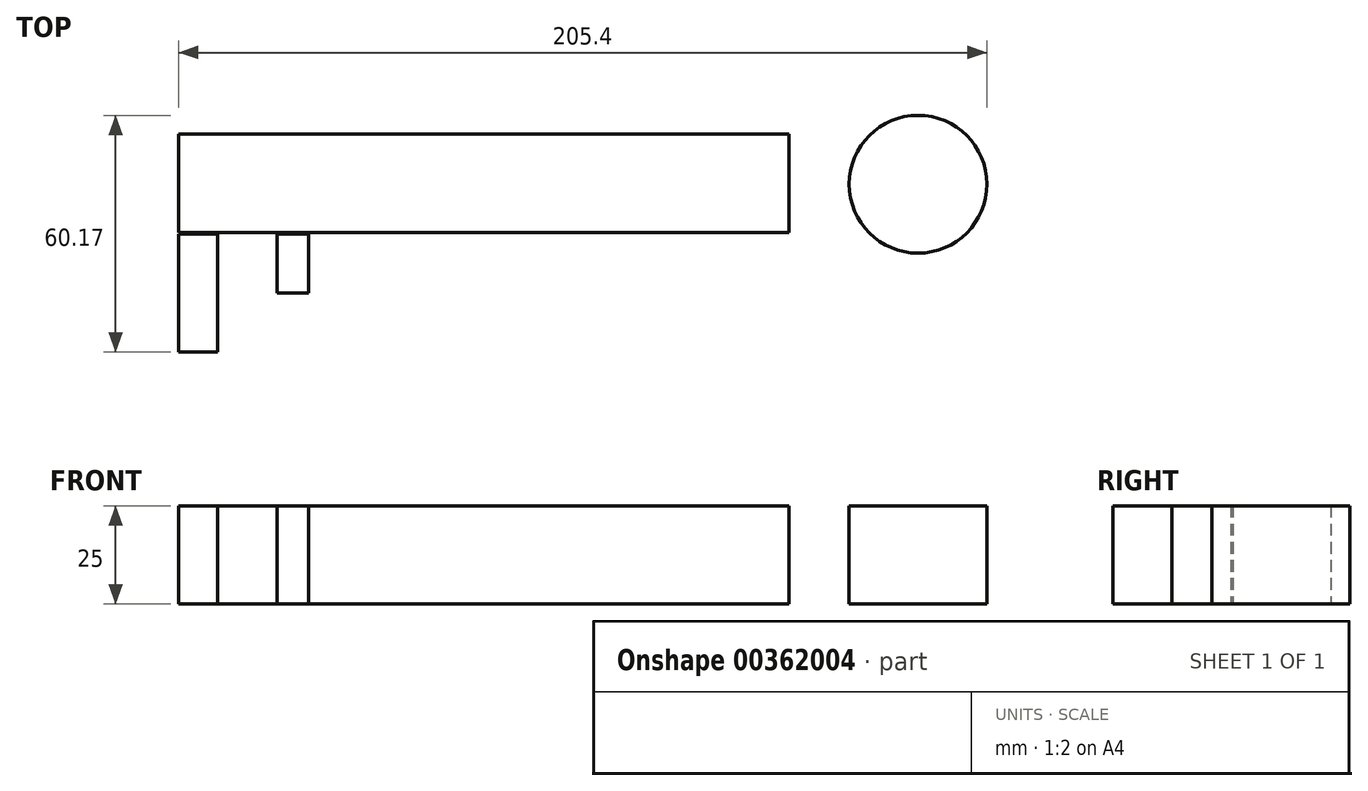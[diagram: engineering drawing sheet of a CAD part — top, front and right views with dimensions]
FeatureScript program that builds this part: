
annotation { "Feature Type Name" : "Feature", "Feature Type Description" : "" }
export const myFeature = defineFeature(function(context is Context, id is Id, definition is map)
    precondition{}
    {
        {
            var Q0;
            Q0=qCreatedBy(makeId("Top.planeOp"),FACE);
            var sketch = newSketch(context, id + "F0", { "sketchPlane" : qUnion([Q0])});
            skLineSegment(sketch, "E0.bottom", {"start": v(-98.68, 48.37) * mm, "end": v(56.32, 48.37) * mm});
            skLineSegment(sketch, "E0.top", {"start": v(-98.68, 23.37) * mm, "end": v(56.32, 23.37) * mm});
            skLineSegment(sketch, "E0.left", {"start": v(-98.68, 48.37) * mm, "end": v(-98.68, 23.37) * mm});
            skLineSegment(sketch, "E0.right", {"start": v(56.32, 48.37) * mm, "end": v(56.32, 23.37) * mm});
            skSolve(sketch);
        }
        {
            var Q0;
            Q0=qCreatedBy(makeId("Top.planeOp"),FACE);
            var sketch = newSketch(context, id + "F1", { "sketchPlane" : qUnion([Q0])});
            skArc(sketch, "E1", {"start": v(56.43, 23.25) * mm, "mid": v(124.16, 35.24) * mm, "end": v(56.7, 48.72) * mm});
            skLineSegment(sketch, "E2.bottom", {"start": v(-98.73, 22.95) * mm, "end": v(-88.73, 22.95) * mm});
            skLineSegment(sketch, "E2.top", {"start": v(-98.73, -7.05) * mm, "end": v(-88.73, -7.05) * mm});
            skLineSegment(sketch, "E2.left", {"start": v(-98.73, 22.95) * mm, "end": v(-98.73, -7.05) * mm});
            skLineSegment(sketch, "E2.right", {"start": v(-88.73, 22.95) * mm, "end": v(-88.73, -7.05) * mm});
            skLineSegment(sketch, "E3.bottom", {"start": v(-88.73, 22.95) * mm, "end": v(-73.73, 22.95) * mm});
            skLineSegment(sketch, "E3.top", {"start": v(-88.73, 22.95) * mm, "end": v(-73.73, 22.95) * mm});
            skLineSegment(sketch, "E3.left", {"start": v(-88.73, 22.95) * mm, "end": v(-88.73, 22.95) * mm});
            skLineSegment(sketch, "E3.right", {"start": v(-73.73, 22.95) * mm, "end": v(-73.73, 22.95) * mm});
            skLineSegment(sketch, "E4.bottom", {"start": v(-73.73, 22.95) * mm, "end": v(-65.73, 22.95) * mm});
            skLineSegment(sketch, "E4.top", {"start": v(-73.73, 7.95) * mm, "end": v(-65.73, 7.95) * mm});
            skLineSegment(sketch, "E4.left", {"start": v(-73.73, 22.95) * mm, "end": v(-73.73, 7.95) * mm});
            skLineSegment(sketch, "E4.right", {"start": v(-65.73, 22.95) * mm, "end": v(-65.73, 7.95) * mm});
            skCircle(sketch, "E5", {"center": v(89.17, 35.62) * mm, "radius": 17.5 * mm});
            skLineSegment(sketch, "E6", {"start": v(-54.7, 23.35) * mm, "end": v(-49.47, 7.64) * mm});
            skLineSegment(sketch, "E7", {"start": v(-49.47, 7.64) * mm, "end": v(-43.17, 22.95) * mm});
            skLineSegment(sketch, "E8", {"start": v(113.24, 61.03) * mm, "end": v(101.2, 48.33) * mm});
            skSolve(sketch);
        }
        {
            var Q0;
            Q0 = qSketchRegion(id + "F1", true);
            var Q1;
            Q1=makeQuery(id+"F0.imprint","IMPRINT",FACE,{"disambiguationData":[TD([[makeQuery(id+"F0.imprint","IMPRINT",EDGE,{"derivedFrom":sQuery(id+"F0.wireOp",EDGE,"E0.bottom")}),-1.0]])]});
            extrude(context, id + "F2", {"entities" : qUnion([Q0, Q1]), "depth" : 25 * mm});
        }
    });
